# Revit family: CSL49 6
name_source: partatom
category: Aparatos eléctricos
revit_build: Autodesk Revit 2016 (Build: 20150220_1215(x64)
units: mm (PartAtom-declared; Revit-internal decimal feet)

## family parameters
Anfitrión = Cara
Compartido = No
Corte con vacíos al cargar = No
Cota de conector redondo = Diámetro de uso
Mantener orientación de anotación = No
Número OmniClass = 23.80.50.11.11
Punto de cálculo de habitación = No
Tipo de pieza = Normal
Título OmniClass = Receptacle Terminal Units

## types (2) — shared parameters
CSL 4 (AltoxLargoxAncho) = 45 x 130 x 190 mm
Capacidad = 4 módulos PLUS
Compatibilidad = Gama 45
Composición = Cubeta, Tapa, Tornillería tapa (2ud), Tornillería montaje en suelo (4ud), Entrada lateral 2 conectores CR, Entrada ciega
Código de montaje = D5020100
Descripción = Caja de conexiones de red en suelo CSL 4
Elevación por defecto = 1200 mm
Fabricante = MMCONECTA
Instalación = En suelo
Materia prima = Policarbonato libre de halógenos
Modelo = CSL 4
Normativas = UNE 60670-1:2006 + CORR. 2008 / Marcado CE
URL = http://www.mmconecta.com

## per-type parameters (varying)
| type | Acabado |
| Módulo /4 - Blanco | Blanco nieve RAL9019 |
| Módulo /6 - Grafito | Grafito RAL7021 |

## geometry (parser evidence)
native form markers: Blend x4
no freeform markers — native parametric forms only
